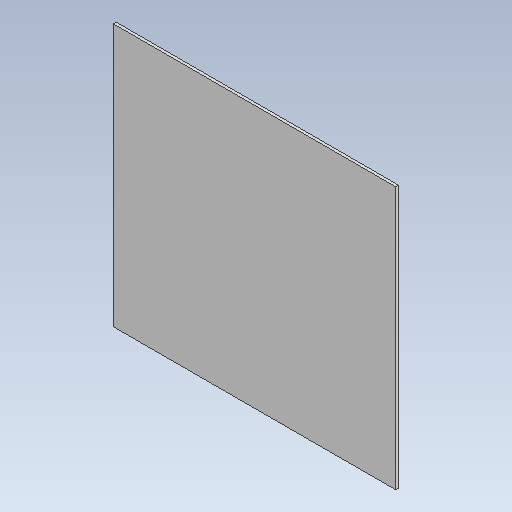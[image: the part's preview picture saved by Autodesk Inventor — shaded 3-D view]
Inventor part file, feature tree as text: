
AUTODESK INVENTOR PART (.ipt)
format: ipt  version: 2020.3 (Build 243373010, 373A)  size: 168,960 bytes
history: native  units: mm
features: other x32, plane x1, extrude x1, sketch x1
ambient origin geometry x8: Origin, YZ Plane, XZ Plane, XY Plane, X Axis, Y Axis, Z Axis, Center Point
bodies: Solid1 (feature_tree)
feature tree (35):
  other  "base_sketch.ipt"
  plane  "Work Plane1"
  extrude  "Extrusion1"  Depth=1.2mm
  other  "bulkhead_main"
  other  "bulkhead_F1"
  other  "bulkhead_front"
  other  "bulkhead_F2"
  other  "bulkhead_B1"
  other  "bulkhead_B2"
  other  "transom"
  other  "stinger_bottom_liner"
  other  "bulkhead_front_tunnel_top"
  other  "bulkhead_front_tunnel_bottom"
  other  "bulkhead_main_top"
  other  "bulkhead_main_tunnel_bottom"
  other  "bulkhead_main_tunnel_standoff"
  other  "bulkhead_front_top"
  other  "bulkhead_front_bottom"
  other  "bulkhead_F1_tunnel_bottom"
  other  "bulkhead_F1_tunnel_top"
  other  "bulkhead_F1_top"
  other  "bulkhead_F1_tunnel_standoff"
  other  "bulkhead_F1_bottom"
  other  "bulkhead_F2_bottom"
  other  "bulkhead_F2_top"
  other  "bulkhead_B1_bottom"
  other  "bulkhead_B1_top"
  other  "bulkhead_B1_tunnel_standoff"
  other  "bulkhead_B1_tunnel_bottom"
  other  "bulkhead_B2_top"
  other  "bulkhead_B2_tunnel_bottom"
  other  "bulkhead_B2_bottom"
  other  "stringer"
  other  "stringer_inside"
  sketch  "Sketch11"  dims[d0=10.0mm d2=35.7mm d3=20.4mm d7=204.0mm d24=45.9mm d27=11.475mm d41=45.9mm d44=0.698132mm d45=122.4mm d48=27.54mm d50=49.7352mm d51=43.146mm d53=62.322mm d54=119.85mm d56=34.5168mm d57=11.5056mm d58=2.48676mm d61=33.558mm d63=0.918mm d66=62.322mm d67=19.176mm d68=19.176mm d70=9.18mm d71=15.0552mm d84=153.0mm d85=41.6925mm d86=102.0mm d87=42.84mm d90=40.8mm d91=24.48mm d95=10.2mm d97=10.340551mm d98=15.510827mm d100=8.541983mm d101=2.55mm d103=112.2mm d104=6.40305mm d105=6.885mm d106=17.2125mm d108=12.202833mm d110=3.582087mm d111=-102.0mm d112=-204.0mm d114=6.981317mm d115=6.981317mm d116=6.981317mm d119=11.760494mm d121=3.635062mm d123=0.729849mm d124=0.364924mm d126=2.390472mm d127=1.195236mm d131=48.8988mm d137=1.86507mm d30=306.0mm d49=45.9mm d55=57.528mm d64=19.176mm d65=18.36mm d96=34.468504mm d99=12.202833mm d107=12.202833mm d109=3.582087mm d120=21.382716mm d122=1.094773mm d125=3.585707mm d128=6.375647mm d130=57.528mm d136=2.48676mm d1=1.2mm d4=0.0mm d5=2.0mm]
